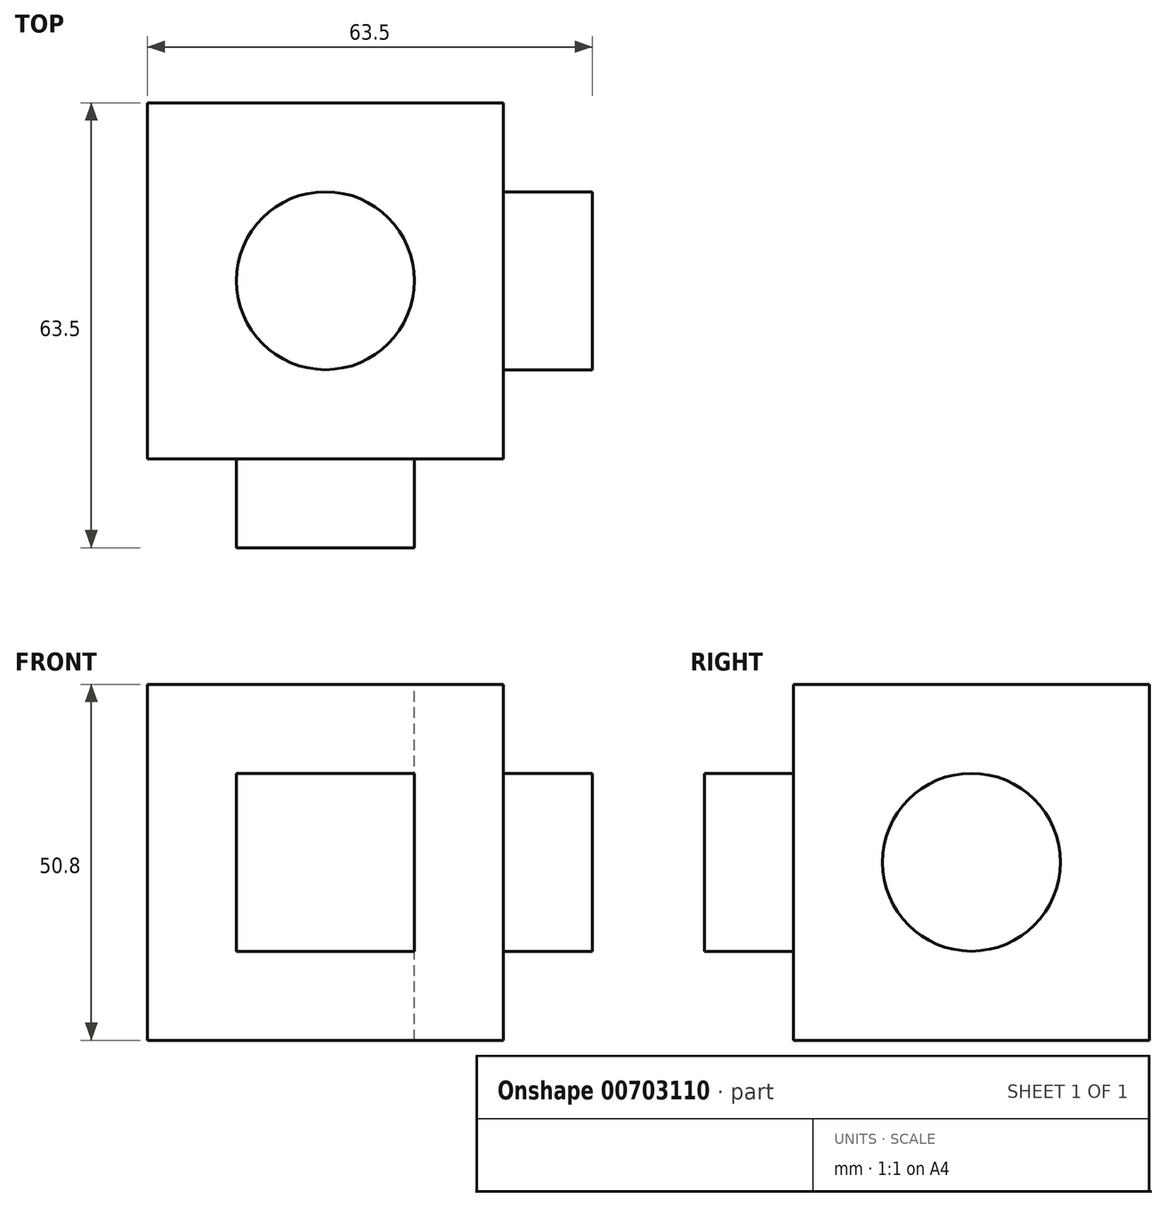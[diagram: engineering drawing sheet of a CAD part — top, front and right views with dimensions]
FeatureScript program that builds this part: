
annotation { "Feature Type Name" : "Feature", "Feature Type Description" : "" }
export const myFeature = defineFeature(function(context is Context, id is Id, definition is map)
    precondition{}
    {
        {
            var Q0;
            Q0=qCreatedBy(makeId("Front.planeOp"),FACE);
            var sketch = newSketch(context, id + "F0", { "sketchPlane" : qUnion([Q0])});
            skLineSegment(sketch, "E0.bottom", {"start": v(-34.47, -18.05) * mm, "end": v(16.33, -18.05) * mm});
            skLineSegment(sketch, "E0.top", {"start": v(-34.47, 32.75) * mm, "end": v(16.33, 32.75) * mm});
            skLineSegment(sketch, "E0.left", {"start": v(-34.47, -18.05) * mm, "end": v(-34.47, 32.75) * mm});
            skLineSegment(sketch, "E0.right", {"start": v(16.33, -18.05) * mm, "end": v(16.33, 32.75) * mm});
            skSolve(sketch);
        }
        {
            var Q0;
            Q0 = qSketchRegion(id + "F0", true);
            extrude(context, id + "F1", {"entities" : qUnion([Q0]), "depth" : 50.8 * mm, "offsetDistance" : 25.4 * mm});
        }
        {
            var Q0;
            Q0=makeQuery(id+"F1.opExtrude","SWEPT_FACE",FACE,{"disambiguationData":[OSD([sQuery(id+"F0.wireOp",EDGE,"E0.top")])]});
            var sketch = newSketch(context, id + "F2", { "sketchPlane" : qUnion([Q0])});
            skCircle(sketch, "E1", {"center": v(-9.07, -25.4) * mm, "radius": 12.7 * mm});
            skSolve(sketch);
        }
        {
            var Q0;
            Q0=makeQuery(id+"F2.imprint","IMPRINT",FACE,{"disambiguationData":[TD([[makeQuery(id+"F2.imprint","IMPRINT",EDGE,{"derivedFrom":sQuery(id+"F2.wireOp",EDGE,"E1")}),1.0]])]});
            extrude(context, id + "F3", {"entities" : qUnion([Q0]), "operationType" : NewBodyOperationType.REMOVE, "oppositeDirection" : true, "depth" : 50.8 * mm, "offsetDistance" : 25.4 * mm});
        }
        {
            var Q0;
            Q0=makeQuery(id+"F1.opExtrude","CAP_FACE",FACE,{"disambiguationData":[OSD([sQuery(id+"F0.wireOp",EDGE,"E0.bottom"),sQuery(id+"F0.wireOp",EDGE,"E0.top"),sQuery(id+"F0.wireOp",EDGE,"E0.left"),sQuery(id+"F0.wireOp",EDGE,"E0.right")])],"isStart":false});
            var sketch = newSketch(context, id + "F4", { "sketchPlane" : qUnion([Q0])});
            skLineSegment(sketch, "E2.bottom", {"start": v(-21.77, 20.05) * mm, "end": v(3.63, 20.05) * mm});
            skLineSegment(sketch, "E2.top", {"start": v(-21.77, -5.35) * mm, "end": v(3.63, -5.35) * mm});
            skLineSegment(sketch, "E2.left", {"start": v(-21.77, 20.05) * mm, "end": v(-21.77, -5.35) * mm});
            skLineSegment(sketch, "E2.right", {"start": v(3.63, 20.05) * mm, "end": v(3.63, -5.35) * mm});
            skSolve(sketch);
        }
        {
            var Q0;
            Q0 = qSketchRegion(id + "F4", true);
            extrude(context, id + "F5", {"entities" : qUnion([Q0]), "operationType" : NewBodyOperationType.ADD, "depth" : 12.7 * mm, "offsetDistance" : 25.4 * mm});
        }
        {
            var Q0;
            Q0=makeQuery(id+"F1.opExtrude","SWEPT_FACE",FACE,{"disambiguationData":[OSD([sQuery(id+"F0.wireOp",EDGE,"E0.right")])]});
            var sketch = newSketch(context, id + "F6", { "sketchPlane" : qUnion([Q0])});
            skCircle(sketch, "E3", {"center": v(-25.4, 7.35) * mm, "radius": 12.7 * mm});
            skSolve(sketch);
        }
        {
            var Q0;
            Q0=makeQuery(id+"F6.imprint","IMPRINT",FACE,{"disambiguationData":[TD([[makeQuery(id+"F6.imprint","IMPRINT",EDGE,{"derivedFrom":sQuery(id+"F6.wireOp",EDGE,"E3")}),1.0]])]});
            extrude(context, id + "F7", {"entities" : qUnion([Q0]), "operationType" : NewBodyOperationType.ADD, "depth" : 12.7 * mm, "offsetDistance" : 25.4 * mm});
        }
    });
